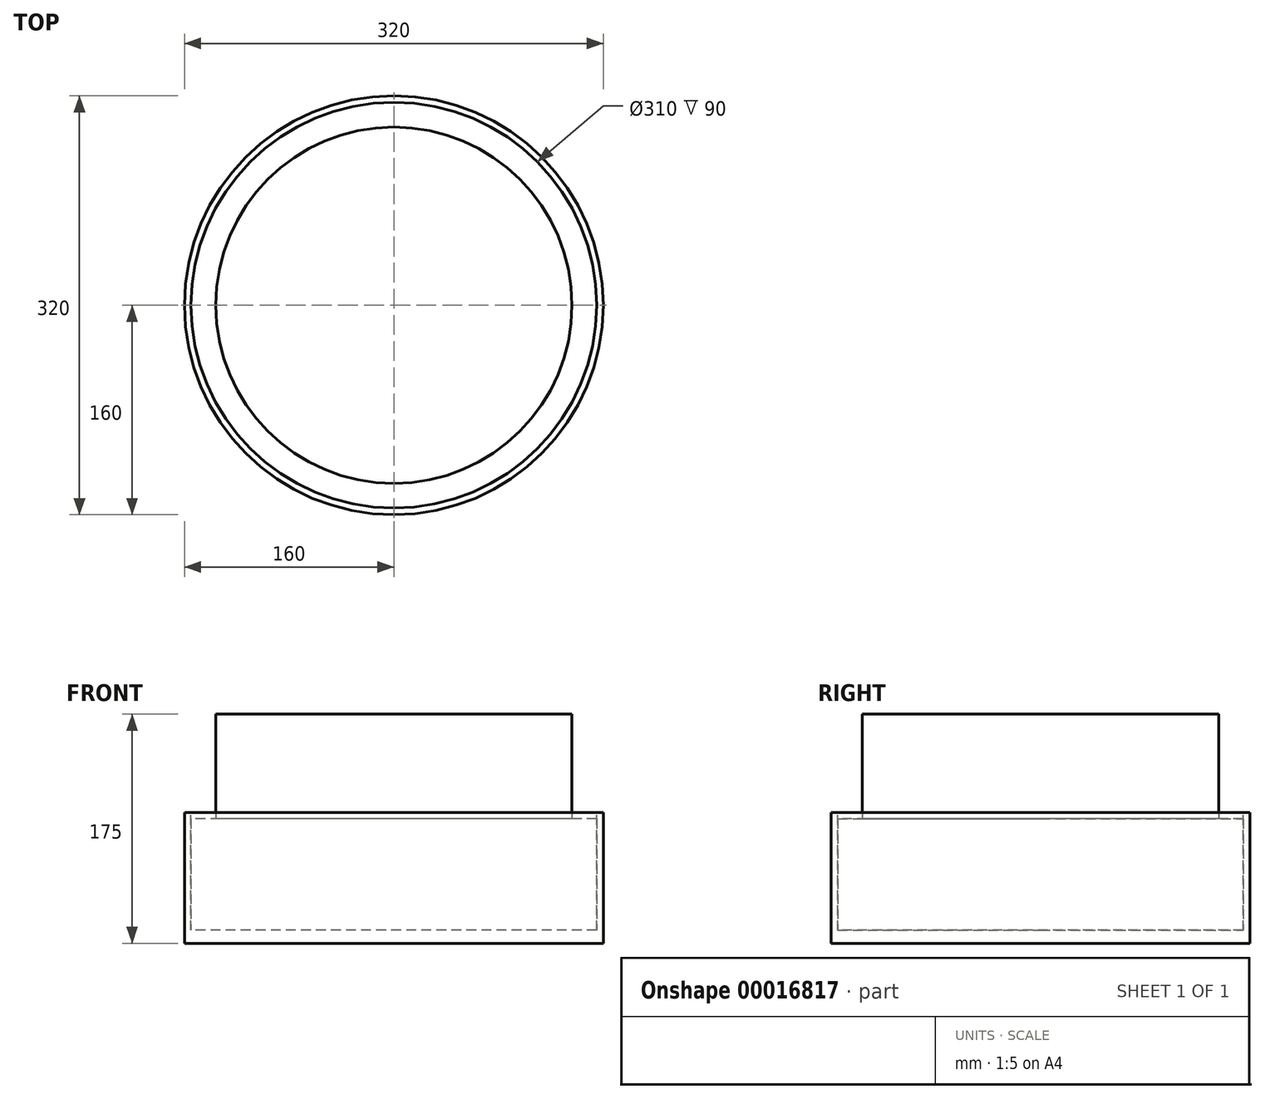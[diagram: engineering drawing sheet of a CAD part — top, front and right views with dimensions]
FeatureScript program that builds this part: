
annotation { "Feature Type Name" : "Feature", "Feature Type Description" : "" }
export const myFeature = defineFeature(function(context is Context, id is Id, definition is map)
    precondition{}
    {
        {
            var Q0;
            Q0=qCreatedBy(makeId("Top.planeOp"),FACE);
            var sketch = newSketch(context, id + "F0", { "sketchPlane" : qUnion([Q0])});
            skCircle(sketch, "E0", {"center": v(0, 0) * mm, "radius": 160 * mm});
            skSolve(sketch);
        }
        {
            var Q0;
            Q0 = qSketchRegion(id + "F0", true);
            extrude(context, id + "F1", {"entities" : qUnion([Q0]), "depth" : 100 * mm});
        }
        {
            var Q0;
            Q0=makeQuery(id+"F1.opExtrude","CAP_FACE",FACE,{"disambiguationData":[OSD([sQuery(id+"F0.wireOp",EDGE,"E0")])],"isStart":false});
            var sketch = newSketch(context, id + "F2", { "sketchPlane" : qUnion([Q0])});
            skCircle(sketch, "E1", {"center": v(0, 0) * mm, "radius": 155 * mm});
            skSolve(sketch);
        }
        {
            var Q0;
            Q0 = qSketchRegion(id + "F2", true);
            extrude(context, id + "F3", {"entities" : qUnion([Q0]), "operationType" : NewBodyOperationType.REMOVE, "oppositeDirection" : true, "depth" : 90 * mm});
        }
        {
            var Q0;
            Q0=makeQuery(id+"F3.boolean.opBoolean","COPY",FACE,{"derivedFrom":makeQuery(id+"F3.opExtrude","CAP_FACE",FACE,{"disambiguationData":[OSD([sQuery(id+"F2.wireOp",EDGE,"E1")])],"isStart":false})});
            extrude(context, id + "F4", {"entities" : qUnion([Q0]), "depth" : 85 * mm});
        }
        {
            var Q0;
            Q0=makeQuery(id+"F4.opExtrude","CAP_FACE",FACE,{"disambiguationData":[OSD([sQuery(id+"F2.wireOp",EDGE,"E1")])],"isStart":false});
            var sketch = newSketch(context, id + "F5", { "sketchPlane" : qUnion([Q0])});
            skCircle(sketch, "E2", {"center": v(0, 0) * mm, "radius": 2.5 * mm});
            skSolve(sketch);
        }
        {
            var Q0;
            Q0=makeQuery(id+"F4.opExtrude","CAP_FACE",FACE,{"disambiguationData":[OSD([sQuery(id+"F2.wireOp",EDGE,"E1")])],"isStart":false});
            var sketch = newSketch(context, id + "F6", { "sketchPlane" : qUnion([Q0])});
            skCircle(sketch, "E3", {"center": v(0, 0) * mm, "radius": 136.13 * mm});
            skSolve(sketch);
        }
        {
            var Q0;
            Q0 = qSketchRegion(id + "F6", true);
            extrude(context, id + "F7", {"entities" : qUnion([Q0]), "depth" : 80 * mm});
        }
    });
